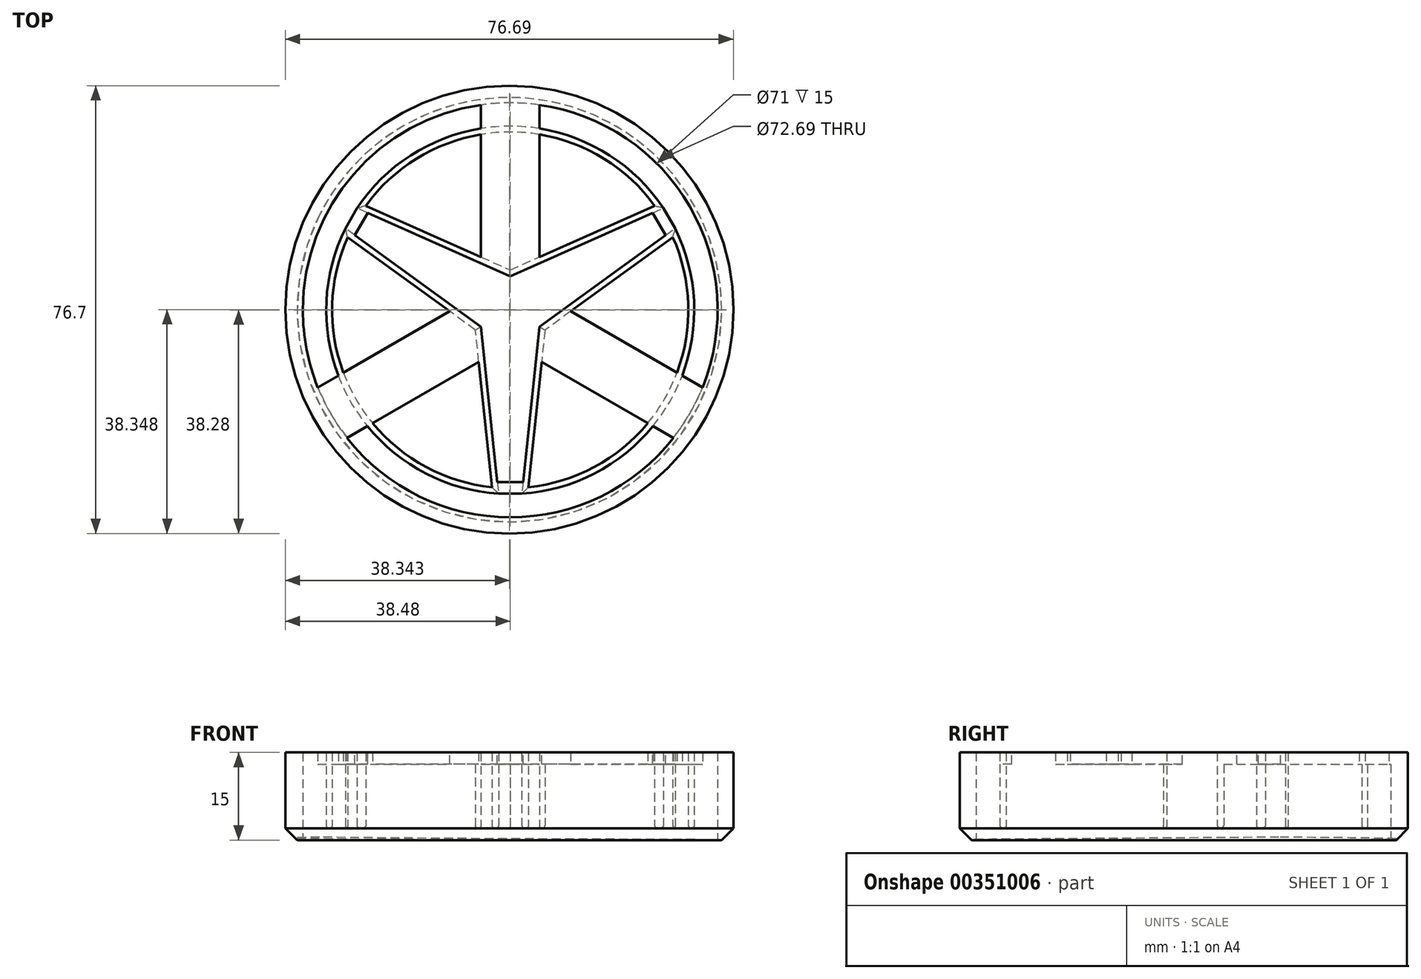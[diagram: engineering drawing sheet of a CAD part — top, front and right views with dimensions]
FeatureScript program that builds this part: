
annotation { "Feature Type Name" : "Feature", "Feature Type Description" : "" }
export const myFeature = defineFeature(function(context is Context, id is Id, definition is map)
    precondition{}
    {
        {
            var Q0;
            Q0=qCreatedBy(makeId("Top.planeOp"),FACE);
            var sketch = newSketch(context, id + "F0", { "sketchPlane" : qUnion([Q0])});
            skCircle(sketch, "E0", {"center": v(0, 0) * mm, "radius": 36.5 * mm});
            skSolve(sketch);
        }
        {
            var Q0;
            Q0 = qSketchRegion(id + "F0", true);
            extrude(context, id + "F1", {"entities" : qUnion([Q0]), "depth" : 20 * mm});
        }
        {
            var Q0;
            Q0=makeQuery(id+"F1.opExtrude","CAP_FACE",FACE,{"disambiguationData":[OSD([sQuery(id+"F0.wireOp",EDGE,"E0")])],"isStart":true});
            var sketch = newSketch(context, id + "F2", { "sketchPlane" : qUnion([Q0])});
            skCircle(sketch, "E1", {"center": v(0, 0) * mm, "radius": 35.5 * mm});
            skCircle(sketch, "E2", {"center": v(0, 0) * mm, "radius": 31.5 * mm});
            skSolve(sketch);
        }
        {
            var Q0;
            Q0 = qSketchRegion(id + "F2", true);
            extrude(context, id + "F3", {"entities" : qUnion([Q0]), "operationType" : NewBodyOperationType.REMOVE, "endBound" : BoundingType.THROUGH_ALL, "oppositeDirection" : true, "depth" : 25 * mm});
        }
        {
            var Q0;
            Q0=makeQuery(id+"F3.boolean.opBoolean","SPLIT",FACE,{"disambiguationData":[TD([makeQuery(id+"F3.opExtrude","SWEPT_FACE",FACE,{"disambiguationData":[OSD([sQuery(id+"F2.wireOp",EDGE,"E2")])]})])],"derivedFrom":makeQuery(id+"F1.opExtrude","CAP_FACE",FACE,{"disambiguationData":[OSD([sQuery(id+"F0.wireOp",EDGE,"E0")])],"isStart":true})});
            var sketch = newSketch(context, id + "F4", { "sketchPlane" : qUnion([Q0])});
            skLineSegment(sketch, "E3", {"start": v(0, 0) * mm, "end": v(0, 31.5) * mm});
            skLineSegment(sketch, "E4.1.0", {"start": v(0, 0) * mm, "end": v(-27.28, -15.75) * mm});
            skLineSegment(sketch, "E4.2.0", {"start": v(0, 0) * mm, "end": v(27.28, -15.75) * mm});
            skPoint(sketch, "E4.center", {"position": v(0, 0) * mm});
            skLineSegment(sketch, "E5", {"start": v(0, 0) * mm, "end": v(-5, 2.89) * mm});
            skLineSegment(sketch, "E6", {"start": v(-5, 2.89) * mm, "end": v(-2, 31.44) * mm});
            skLineSegment(sketch, "E7.MirrorCS", {"start": v(5, 2.89) * mm, "end": v(2, 31.44) * mm});
            skLineSegment(sketch, "E8.1.0", {"start": v(0, -5.77) * mm, "end": v(-26.23, -17.45) * mm});
            skLineSegment(sketch, "E8.1.1", {"start": v(-5, 2.89) * mm, "end": v(-28.22, -13.99) * mm});
            skLineSegment(sketch, "E8.2.0", {"start": v(5, 2.89) * mm, "end": v(28.22, -13.99) * mm});
            skLineSegment(sketch, "E8.2.1", {"start": v(0, -5.77) * mm, "end": v(26.23, -17.45) * mm});
            skSolve(sketch);
        }
        {
            var Q0;
            {var subQ0=sQuery(id+"F4.wireOp",EDGE,"E3");Q0=makeQuery(id+"F4.imprint","IMPRINT",FACE,{"disambiguationData":[TD([[makeQuery(id+"F4.imprint","IMPRINT",EDGE,{"derivedFrom":subQ0}),1.0]])]});}
            var Q1;
            {var subQ3=sQuery(id+"F4.wireOp",EDGE,"E3");Q1=makeQuery(id+"F4.imprint","IMPRINT",FACE,{"disambiguationData":[TD([[makeQuery(id+"F4.imprint","IMPRINT",EDGE,{"derivedFrom":subQ3}),-1.0]])]});}
            var Q2;
            {var subQ0=sQuery(id+"F4.wireOp",EDGE,"E4.1.0");Q2=makeQuery(id+"F4.imprint","IMPRINT",FACE,{"disambiguationData":[TD([[makeQuery(id+"F4.imprint","IMPRINT",EDGE,{"derivedFrom":subQ0}),-1.0]])]});}
            var Q3;
            {var subQ3=sQuery(id+"F4.wireOp",EDGE,"E4.1.0");Q3=makeQuery(id+"F4.imprint","IMPRINT",FACE,{"disambiguationData":[TD([[makeQuery(id+"F4.imprint","IMPRINT",EDGE,{"derivedFrom":subQ3}),1.0]])]});}
            extrude(context, id + "F5", {"entities" : qUnion([Q0, Q1, Q2, Q3]), "operationType" : NewBodyOperationType.REMOVE, "endBound" : BoundingType.THROUGH_ALL, "oppositeDirection" : true, "depth" : 25 * mm});
        }
        {
            var Q0;
            {var subQ0=makeQuery(id+"F3.opExtrude","SWEPT_FACE",FACE,{"disambiguationData":[OSD([sQuery(id+"F2.wireOp",EDGE,"E2")])]});Q0=makeQuery(id+"F5.boolean.opBoolean","SPLIT",FACE,{"disambiguationData":[TD([makeQuery(id+"F5.opExtrude","SWEPT_FACE",FACE,{"disambiguationData":[OSD([sQuery(id+"F4.wireOp",EDGE,"E6")])]})])],"derivedFrom":makeQuery(id+"F3.boolean.opBoolean","SPLIT",FACE,{"disambiguationData":[TD([subQ0])],"derivedFrom":makeQuery(id+"F1.opExtrude","CAP_FACE",FACE,{"disambiguationData":[OSD([sQuery(id+"F0.wireOp",EDGE,"E0")])],"isStart":true})})});}
            var sketch = newSketch(context, id + "F6", { "sketchPlane" : qUnion([Q0])});
            skCircle(sketch, "E9", {"center": v(0, 0) * mm, "radius": 31.5 * mm});
            skSolve(sketch);
        }
        {
            var Q0;
            Q0=makeQuery(id+"F6.imprint","IMPRINT",FACE,{"disambiguationData":[TD([[makeQuery(id+"F6.imprint","IMPRINT",EDGE,{"disambiguationData":[OD(0.0)],"derivedFrom":sQuery(id+"F6.wireOp",EDGE,"E9")}),1.0]])]});
            var sketch = newSketch(context, id + "F7", { "sketchPlane" : qUnion([Q0])});
            skLineSegment(sketch, "E10", {"start": v(-3.12, 30.34) * mm, "end": v(-5.95, 3.43) * mm});
            skLineSegment(sketch, "E11", {"start": v(-5.95, 3.43) * mm, "end": v(-27.84, -12.47) * mm});
            skArc(sketch, "E12", {"start": v(-3.12, 30.34) * mm, "mid": v(-26.41, 15.25) * mm, "end": v(-27.84, -12.47) * mm});
            skPoint(sketch, "E13.orphan", {"position": v(-3.01, 31.36) * mm});
            skPoint(sketch, "E14.orphan", {"position": v(-28.66, -13.07) * mm});
            skLineSegment(sketch, "E15", {"start": v(0, 0) * mm, "end": v(0, 33.4) * mm});
            skLineSegment(sketch, "E16", {"start": v(0, 33.4) * mm, "end": v(10.75, 31.74) * mm});
            skLineSegment(sketch, "E17", {"start": v(10.75, 31.74) * mm, "end": v(25.48, 23.28) * mm});
            skLineSegment(sketch, "E18", {"start": v(25.48, 23.28) * mm, "end": v(32.74, 6.68) * mm});
            skLineSegment(sketch, "E19", {"start": v(32.74, 6.68) * mm, "end": v(32.74, -5.75) * mm});
            skLineSegment(sketch, "E20", {"start": v(32.74, -5.75) * mm, "end": v(26.58, -22.02) * mm});
            skLineSegment(sketch, "E21", {"start": v(26.58, -22.02) * mm, "end": v(14.18, -31.03) * mm});
            skLineSegment(sketch, "E22", {"start": v(14.18, -31.03) * mm, "end": v(-5.52, -33.45) * mm});
            skLineSegment(sketch, "E23", {"start": v(-5.52, -33.45) * mm, "end": v(-19.15, -28.06) * mm});
            skLineSegment(sketch, "E24", {"start": v(-19.15, -28.06) * mm, "end": v(-27.07, -19.82) * mm});
            skLineSegment(sketch, "E25", {"start": v(-27.07, -19.82) * mm, "end": v(-27.07, -15.53) * mm});
            skLineSegment(sketch, "E26", {"start": v(-27.07, -15.53) * mm, "end": v(0, 0) * mm});
            skSolve(sketch);
        }
        {
            var Q0;
            Q0 = qSketchRegion(id + "F7", true);
            extrude(context, id + "F8", {"entities" : qUnion([Q0]), "operationType" : NewBodyOperationType.REMOVE, "endBound" : BoundingType.THROUGH_ALL, "oppositeDirection" : true, "depth" : 25 * mm});
        }
        {
            var Q0;
            Q0=qCreatedBy(makeId("Right.planeOp"),FACE);
            var sketch = newSketch(context, id + "F9", { "sketchPlane" : qUnion([Q0])});
            skLineSegment(sketch, "E27", {"start": v(0, -25.69) * mm, "end": v(0, 43.38) * mm});
            skSolve(sketch);
        }
        {
            var Q0;
            Q0=makeQuery(id+"F5.boolean.opBoolean","SPLIT",BODY,{"disambiguationData":[OD(0.0)],"derivedFrom":makeQuery(id+"F3.boolean.opBoolean","SPLIT",BODY,{"disambiguationData":[OD(1.0)],"derivedFrom":makeQuery(id+"F1.opExtrude","SWEPT_BODY",BODY,{"disambiguationData":[OSD([sQuery(id+"F0.wireOp",EDGE,"E0")])]})})});
            var Q1;
            Q1=sQuery(id+"F9.wireOp",EDGE,"E27");
            circularPattern(context, id + "F10", {"entities" : qUnion([Q0]), "axis" : qUnion([Q1]), "angle" : 360 * degree, "instanceCount" : 3, "equalSpace" : true});
        }
        {
            var Q0;
            Q0=qCreatedBy(makeId("Top.planeOp"),FACE);
            var sketch = newSketch(context, id + "F11", { "sketchPlane" : qUnion([Q0])});
            skCircle(sketch, "E28", {"center": v(0, 0) * mm, "radius": 32.97 * mm});
            skSolve(sketch);
        }
        {
            var Q0;
            Q0 = qSketchRegion(id + "F11", true);
            extrude(context, id + "F12", {"entities" : qUnion([Q0]), "operationType" : NewBodyOperationType.REMOVE, "depth" : 2 * mm});
        }
        {
            var Q0;
            {var subQ0=sQuery(id+"F0.wireOp",EDGE,"E0");Q0=makeQuery(id+"F3.boolean.opBoolean","SPLIT",FACE,{"disambiguationData":[TD([makeQuery(id+"F1.opExtrude","SWEPT_FACE",FACE,{"disambiguationData":[OSD([subQ0])]})])],"derivedFrom":makeQuery(id+"F1.opExtrude","CAP_FACE",FACE,{"disambiguationData":[OSD([subQ0])],"isStart":false})});}
            var sketch = newSketch(context, id + "F13", { "sketchPlane" : qUnion([Q0])});
            skCircle(sketch, "E29", {"center": v(0, 0) * mm, "radius": 36.5 * mm});
            skSolve(sketch);
        }
        {
            var Q0;
            Q0 = qSketchRegion(id + "F13", true);
            extrude(context, id + "F14", {"entities" : qUnion([Q0]), "operationType" : NewBodyOperationType.ADD, "oppositeDirection" : true, "depth" : 5 * mm});
        }
        {
            var Q0;
            Q0=makeQuery(id+"F8.boolean.opBoolean","COPY",EDGE,{"derivedFrom":makeQuery(id+"F8.opExtrude","CAP_EDGE",EDGE,{"disambiguationData":[OSD([sQuery(id+"F7.wireOp",EDGE,"E12")])],"isStart":true})});
            var Q1;
            Q1=makeQuery(id+"F8.boolean.opBoolean","COPY",EDGE,{"derivedFrom":makeQuery(id+"F8.opExtrude","CAP_EDGE",EDGE,{"disambiguationData":[OSD([sQuery(id+"F7.wireOp",EDGE,"E10")])],"isStart":true})});
            var Q2;
            Q2=makeQuery(id+"F8.boolean.opBoolean","COPY",EDGE,{"derivedFrom":makeQuery(id+"F8.opExtrude","CAP_EDGE",EDGE,{"disambiguationData":[OSD([sQuery(id+"F7.wireOp",EDGE,"E11")])],"isStart":true})});
            var Q3;
            Q3=makeQuery(id+"F5.boolean.opBoolean","COPY",EDGE,{"derivedFrom":makeQuery(id+"F5.opExtrude","CAP_EDGE",EDGE,{"disambiguationData":[OSD([sQuery(id+"F4.wireOp",EDGE,"E8.1.1")])],"isStart":true})});
            var Q4;
            Q4=makeQuery(id+"F5.boolean.opBoolean","COPY",EDGE,{"derivedFrom":makeQuery(id+"F5.opExtrude","CAP_EDGE",EDGE,{"disambiguationData":[OSD([sQuery(id+"F4.wireOp",EDGE,"E6")])],"isStart":true})});
            var Q5;
            {var subQ0=sQuery(id+"F2.wireOp",EDGE,"E2");Q5=makeQuery(id+"F5.boolean.opBoolean","SPLIT",EDGE,{"disambiguationData":[TD([makeQuery(id+"F5.opExtrude","SWEPT_FACE",FACE,{"disambiguationData":[OSD([sQuery(id+"F4.wireOp",EDGE,"E6")])]})])],"derivedFrom":makeQuery(id+"F3.boolean.opBoolean","COPY",EDGE,{"derivedFrom":makeQuery(id+"F3.opExtrude","CAP_EDGE",EDGE,{"disambiguationData":[OSD([subQ0])],"isStart":true})})});}
            var Q6;
            Q6=makeQuery(id+"F3.boolean.opBoolean","COPY",EDGE,{"derivedFrom":makeQuery(id+"F3.opExtrude","CAP_EDGE",EDGE,{"disambiguationData":[OSD([sQuery(id+"F2.wireOp",EDGE,"E1")])],"isStart":true})});
            var Q7;
            Q7=makeQuery(id+"F1.opExtrude","CAP_EDGE",EDGE,{"disambiguationData":[OSD([sQuery(id+"F0.wireOp",EDGE,"E0")])],"isStart":true});
            var Q8;
            Q8=makeQuery(id+"F12.boolean.opBoolean","COPY",FACE,{"disambiguationData":[TD([makeQuery(id+"F3.boolean.opBoolean","COPY",FACE,{"derivedFrom":makeQuery(id+"F3.opExtrude","SWEPT_FACE",FACE,{"disambiguationData":[OSD([sQuery(id+"F2.wireOp",EDGE,"E2")])]})})])],"derivedFrom":makeQuery(id+"F12.opExtrude","CAP_FACE",FACE,{"disambiguationData":[OSD([sQuery(id+"F11.wireOp",EDGE,"E28")])],"isStart":false})});
            var Q9;
            {var subQ1=makeQuery(id+"F5.opExtrude","SWEPT_FACE",FACE,{"disambiguationData":[OSD([sQuery(id+"F4.wireOp",EDGE,"E6")])]});Q9=makeQuery(id+"F12.boolean.opBoolean","COPY",FACE,{"disambiguationData":[TD([makeQuery(id+"F10.opPattern","COPY",FACE,{"derivedFrom":makeQuery(id+"F5.boolean.opBoolean","COPY",FACE,{"derivedFrom":subQ1}),"instanceName":"2"})])],"derivedFrom":makeQuery(id+"F12.opExtrude","CAP_FACE",FACE,{"disambiguationData":[OSD([sQuery(id+"F11.wireOp",EDGE,"E28")])],"isStart":false})});}
            var Q10;
            {var subQ1=makeQuery(id+"F5.opExtrude","SWEPT_FACE",FACE,{"disambiguationData":[OSD([sQuery(id+"F4.wireOp",EDGE,"E6")])]});Q10=makeQuery(id+"F12.boolean.opBoolean","COPY",FACE,{"disambiguationData":[TD([makeQuery(id+"F10.opPattern","COPY",FACE,{"derivedFrom":makeQuery(id+"F5.boolean.opBoolean","COPY",FACE,{"derivedFrom":subQ1}),"instanceName":"1"})])],"derivedFrom":makeQuery(id+"F12.opExtrude","CAP_FACE",FACE,{"disambiguationData":[OSD([sQuery(id+"F11.wireOp",EDGE,"E28")])],"isStart":false})});}
            fillet(context, id + "F15", {"entities" : qUnion([Q0, Q1, Q2, Q3, Q4, Q5, Q6, Q7, Q8, Q9, Q10]), "radius" : .5 * mm, "tangentPropagation" : true, "defaultsChanged" : false, "vertexSettings" : [], "allowEdgeOverflow" : false});
        }
        {
            var Q0;
            Q0=qCreatedBy(makeId("Top.planeOp"),FACE);
            var sketch = newSketch(context, id + "F16", { "sketchPlane" : qUnion([Q0])});
            skCircle(sketch, "E30", {"center": v(-0.14, 0.07) * mm, "radius": 38.35 * mm});
            skCircle(sketch, "E31", {"center": v(-0.14, 0.07) * mm, "radius": 36.35 * mm});
            skSolve(sketch);
        }
        {
            var Q0;
            Q0 = qSketchRegion(id + "F16", true);
            extrude(context, id + "F17", {"entities" : qUnion([Q0]), "operationType" : NewBodyOperationType.ADD, "depth" : 20 * mm});
        }
        {
            var Q0;
            Q0=makeQuery(id+"F17.opExtrude","CAP_EDGE",EDGE,{"disambiguationData":[OSD([sQuery(id+"F16.wireOp",EDGE,"E30")])],"isStart":true});
            chamfer(context, id + "F18", {"entities" : qUnion([Q0]), "width" : 2 * mm});
        }
        {
            var Q0;
            {var subQ0=makeQuery(id+"F3.opExtrude","SWEPT_FACE",FACE,{"disambiguationData":[OSD([sQuery(id+"F2.wireOp",EDGE,"E2")])]});var subQ1=sQuery(id+"F0.wireOp",EDGE,"E0");var subQ2=makeQuery(id+"F1.opExtrude","CAP_FACE",FACE,{"disambiguationData":[OSD([subQ1])],"isStart":false});var subQ3=makeQuery(id+"F5.boolean.opBoolean","SPLIT",FACE,{"disambiguationData":[TD([makeQuery(id+"F5.opExtrude","SWEPT_FACE",FACE,{"disambiguationData":[OSD([sQuery(id+"F4.wireOp",EDGE,"E6")])]})])],"derivedFrom":makeQuery(id+"F3.boolean.opBoolean","SPLIT",FACE,{"disambiguationData":[TD([subQ0])],"derivedFrom":subQ2})});Q0=makeQuery(id+"F17.boolean.opBoolean","MERGE",FACE,{"derivedFrom":[makeQuery(id+"F14.boolean.opBoolean","MERGE",FACE,{"derivedFrom":[makeQuery(id+"F3.boolean.opBoolean","SPLIT",FACE,{"disambiguationData":[TD([makeQuery(id+"F1.opExtrude","SWEPT_FACE",FACE,{"disambiguationData":[OSD([subQ1])]})])],"derivedFrom":subQ2}),subQ3,makeQuery(id+"F10.opPattern","COPY",FACE,{"derivedFrom":subQ3,"instanceName":"1"}),makeQuery(id+"F10.opPattern","COPY",FACE,{"derivedFrom":subQ3,"instanceName":"2"}),makeQuery(id+"F14.opExtrude","CAP_FACE",FACE,{"disambiguationData":[OSD([sQuery(id+"F13.wireOp",EDGE,"E29")])],"isStart":true})]}),makeQuery(id+"F17.opExtrude","CAP_FACE",FACE,{"disambiguationData":[OSD([sQuery(id+"F16.wireOp",EDGE,"E30"),sQuery(id+"F16.wireOp",EDGE,"E31")])],"isStart":false})]});}
            var sketch = newSketch(context, id + "F19", { "sketchPlane" : qUnion([Q0])});
            skCircle(sketch, "E32", {"center": v(0, 0) * mm, "radius": 41.05 * mm});
            skSolve(sketch);
        }
        {
            var Q0;
            Q0 = qSketchRegion(id + "F19", true);
            extrude(context, id + "F20", {"entities" : qUnion([Q0]), "operationType" : NewBodyOperationType.REMOVE, "oppositeDirection" : true, "depth" : 5 * mm, "offsetDistance" : 25 * mm});
        }
        {
            var Q0;
            Q0=makeQuery(id+"F20.boolean.opBoolean","COPY",FACE,{"disambiguationData":[TD([makeQuery(id+"F3.boolean.opBoolean","COPY",FACE,{"derivedFrom":makeQuery(id+"F3.opExtrude","SWEPT_FACE",FACE,{"disambiguationData":[OSD([sQuery(id+"F2.wireOp",EDGE,"E2")])]})})])],"derivedFrom":makeQuery(id+"F20.opExtrude","CAP_FACE",FACE,{"disambiguationData":[OSD([sQuery(id+"F19.wireOp",EDGE,"E32")])],"isStart":false})});
            var sketch = newSketch(context, id + "F21", { "sketchPlane" : qUnion([Q0])});
            skPoint(sketch, "E33", {"position": v(-5, -2.89) * mm});
            skPoint(sketch, "E34", {"position": v(0, 5.77) * mm});
            skPoint(sketch, "E35", {"position": v(5, -2.89) * mm});
            skLineSegment(sketch, "E36", {"start": v(-5, -2.89) * mm, "end": v(-31.18, -18) * mm, "construction": true});
            skLineSegment(sketch, "E37", {"start": v(0, 5.77) * mm, "end": v(0, 37.17) * mm, "construction": true});
            skLineSegment(sketch, "E38", {"start": v(5, -2.89) * mm, "end": v(32.22, -18.6) * mm, "construction": true});
            skLineSegment(sketch, "E39", {"start": v(-4.43, -8.33) * mm, "end": v(-28.68, -22.33) * mm});
            skLineSegment(sketch, "E40", {"start": v(-28.68, -22.33) * mm, "end": v(-31.18, -18) * mm});
            skLineSegment(sketch, "E41", {"start": v(-31.18, -18) * mm, "end": v(-33.68, -13.67) * mm});
            skLineSegment(sketch, "E42", {"start": v(-33.68, -13.67) * mm, "end": v(-9.43, 0.33) * mm});
            skLineSegment(sketch, "E43", {"start": v(-9.43, 0.33) * mm, "end": v(-5, -2.89) * mm});
            skLineSegment(sketch, "E44", {"start": v(-5, -2.89) * mm, "end": v(-4.43, -8.33) * mm});
            skLineSegment(sketch, "E45.1.0", {"start": v(28.68, -22.33) * mm, "end": v(4.43, -8.33) * mm});
            skLineSegment(sketch, "E45.1.1", {"start": v(9.43, 0.33) * mm, "end": v(33.68, -13.67) * mm});
            skLineSegment(sketch, "E45.1.2", {"start": v(5, -2.89) * mm, "end": v(9.43, 0.33) * mm});
            skLineSegment(sketch, "E45.1.3", {"start": v(4.43, -8.33) * mm, "end": v(5, -2.89) * mm});
            skLineSegment(sketch, "E45.1.4", {"start": v(33.68, -13.67) * mm, "end": v(31.18, -18) * mm});
            skLineSegment(sketch, "E45.1.5", {"start": v(31.18, -18) * mm, "end": v(28.68, -22.33) * mm});
            skLineSegment(sketch, "E45.2.0", {"start": v(5, 36) * mm, "end": v(5, 8) * mm});
            skLineSegment(sketch, "E45.2.1", {"start": v(-5, 8) * mm, "end": v(-5, 36) * mm});
            skLineSegment(sketch, "E45.2.2", {"start": v(0, 5.77) * mm, "end": v(-5, 8) * mm});
            skLineSegment(sketch, "E45.2.3", {"start": v(5, 8) * mm, "end": v(0, 5.77) * mm});
            skLineSegment(sketch, "E45.2.4", {"start": v(-5, 36) * mm, "end": v(0, 36) * mm});
            skLineSegment(sketch, "E45.2.5", {"start": v(0, 36) * mm, "end": v(5, 36) * mm});
            skPoint(sketch, "E45.center", {"position": v(0, 0) * mm});
            skLineSegment(sketch, "E46", {"start": v(-28.22, 13.99) * mm, "end": v(-26.23, 17.45) * mm});
            skLineSegment(sketch, "E47", {"start": v(-26.23, 17.45) * mm, "end": v(-24.39, 16.63) * mm});
            skLineSegment(sketch, "E48", {"start": v(-24.39, 16.63) * mm, "end": v(-26.6, 12.8) * mm});
            skLineSegment(sketch, "E49", {"start": v(-26.6, 12.8) * mm, "end": v(-28.22, 13.99) * mm});
            skLineSegment(sketch, "E50.1.0", {"start": v(-2.2, -29.44) * mm, "end": v(2.2, -29.44) * mm});
            skLineSegment(sketch, "E50.1.1", {"start": v(-2, -31.44) * mm, "end": v(-2.2, -29.44) * mm});
            skLineSegment(sketch, "E50.1.2", {"start": v(2, -31.44) * mm, "end": v(-2, -31.44) * mm});
            skLineSegment(sketch, "E50.1.3", {"start": v(2.2, -29.44) * mm, "end": v(2, -31.44) * mm});
            skLineSegment(sketch, "E50.2.0", {"start": v(26.6, 12.8) * mm, "end": v(24.39, 16.63) * mm});
            skLineSegment(sketch, "E50.2.1", {"start": v(28.22, 13.99) * mm, "end": v(26.6, 12.8) * mm});
            skLineSegment(sketch, "E50.2.2", {"start": v(26.23, 17.45) * mm, "end": v(28.22, 13.99) * mm});
            skLineSegment(sketch, "E50.2.3", {"start": v(24.39, 16.63) * mm, "end": v(26.23, 17.45) * mm});
            skSolve(sketch);
        }
        {
            var Q0;
            Q0 = qSketchRegion(id + "F21", true);
            extrude(context, id + "F22", {"entities" : qUnion([Q0]), "operationType" : NewBodyOperationType.ADD, "oppositeDirection" : true, "depth" : 2 * mm, "offsetDistance" : 25 * mm});
        }
    });
